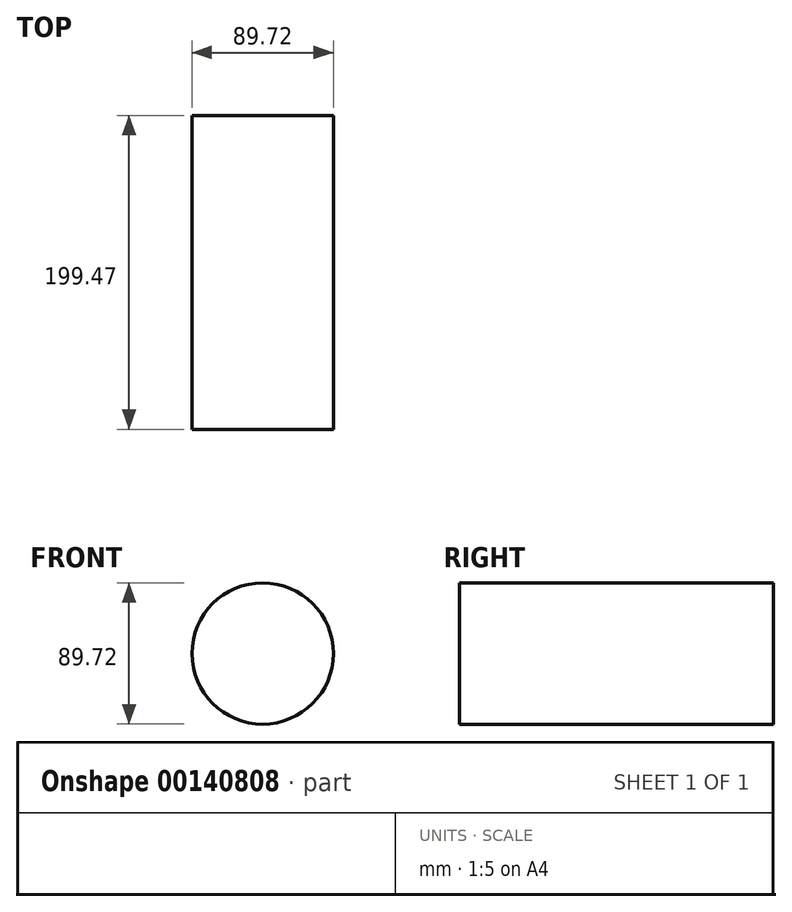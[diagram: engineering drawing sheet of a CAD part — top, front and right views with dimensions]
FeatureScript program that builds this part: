
annotation { "Feature Type Name" : "Feature", "Feature Type Description" : "" }
export const myFeature = defineFeature(function(context is Context, id is Id, definition is map)
    precondition{}
    {
        {
            var Q0;
            Q0=qCreatedBy(makeId("Front.planeOp"),FACE);
            var sketch = newSketch(context, id + "F0", { "sketchPlane" : qUnion([Q0])});
            skCircle(sketch, "E0", {"center": v(0, 0) * mm, "radius": 44.86 * mm});
            skSolve(sketch);
        }
        {
            var Q0;
            Q0=makeQuery(id+"F0.imprint","IMPRINT",FACE,{"disambiguationData":[TD([[makeQuery(id+"F0.imprint","IMPRINT",EDGE,{"derivedFrom":sQuery(id+"F0.wireOp",EDGE,"E0")}),1.0]])]});
            extrude(context, id + "F1", {"entities" : qUnion([Q0]), "depth" : 199.47 * mm});
        }
        {
            var Q0;
            Q0=qCreatedBy(makeId("Right.planeOp"),FACE);
            var sketch = newSketch(context, id + "F2", { "sketchPlane" : qUnion([Q0])});
            skFitSpline(sketch, "E1", {"points": [v(-108.9, 0) * mm, v(-53.1, 33.66) * mm, v(0, 0) * mm, v(-108.9, 0) * mm]});
            skSolve(sketch);
        }
        {
            var Q0;
            Q0=sQuery(id+"F2.wireOp",EDGE,"E1");
            extrude(context, id + "F3", {"bodyType" : ToolBodyType.SURFACE, "surfaceEntities" : qUnion([Q0]), "endBound" : BoundingType.SYMMETRIC, "depth" : 334.35 * mm});
        }
    });
